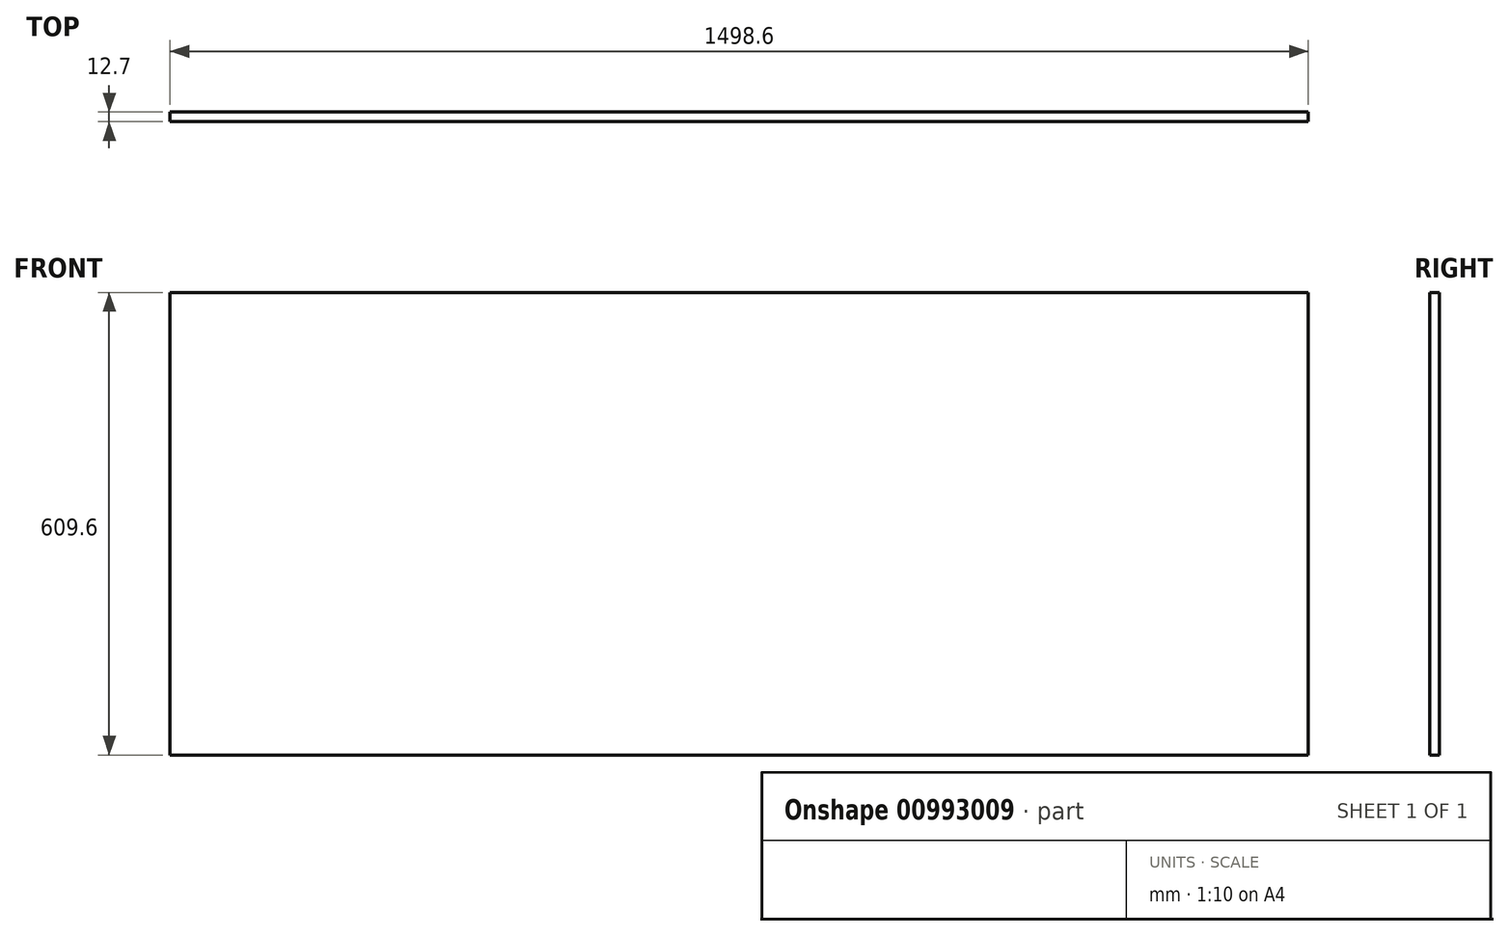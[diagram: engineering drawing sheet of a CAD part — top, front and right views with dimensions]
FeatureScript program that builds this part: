
annotation { "Feature Type Name" : "Feature", "Feature Type Description" : "" }
export const myFeature = defineFeature(function(context is Context, id is Id, definition is map)
    precondition{}
    {
        {
            var Q0;
            Q0=qCreatedBy(makeId("Front.planeOp"),FACE);
            var sketch = newSketch(context, id + "F0", { "sketchPlane" : qUnion([Q0])});
            skLineSegment(sketch, "E0", {"start": v(0, 0) * mm, "end": v(1498.6, 0) * mm});
            skLineSegment(sketch, "E1", {"start": v(0, 0) * mm, "end": v(0, 609.6) * mm});
            skLineSegment(sketch, "E2", {"start": v(0, 609.6) * mm, "end": v(1498.6, 609.6) * mm});
            skLineSegment(sketch, "E3", {"start": v(1498.6, 609.6) * mm, "end": v(1498.6, 0) * mm});
            skSolve(sketch);
        }
        {
            var Q0;
            Q0=makeQuery(id+"F0.imprint","IMPRINT",FACE,{"disambiguationData":[TD([[makeQuery(id+"F0.imprint","IMPRINT",EDGE,{"derivedFrom":sQuery(id+"F0.wireOp",EDGE,"E0")}),1.0]])]});
            extrude(context, id + "F1", {"entities" : qUnion([Q0]), "depth" : 12.7 * mm, "offsetDistance" : 25.4 * mm});
        }
    });
